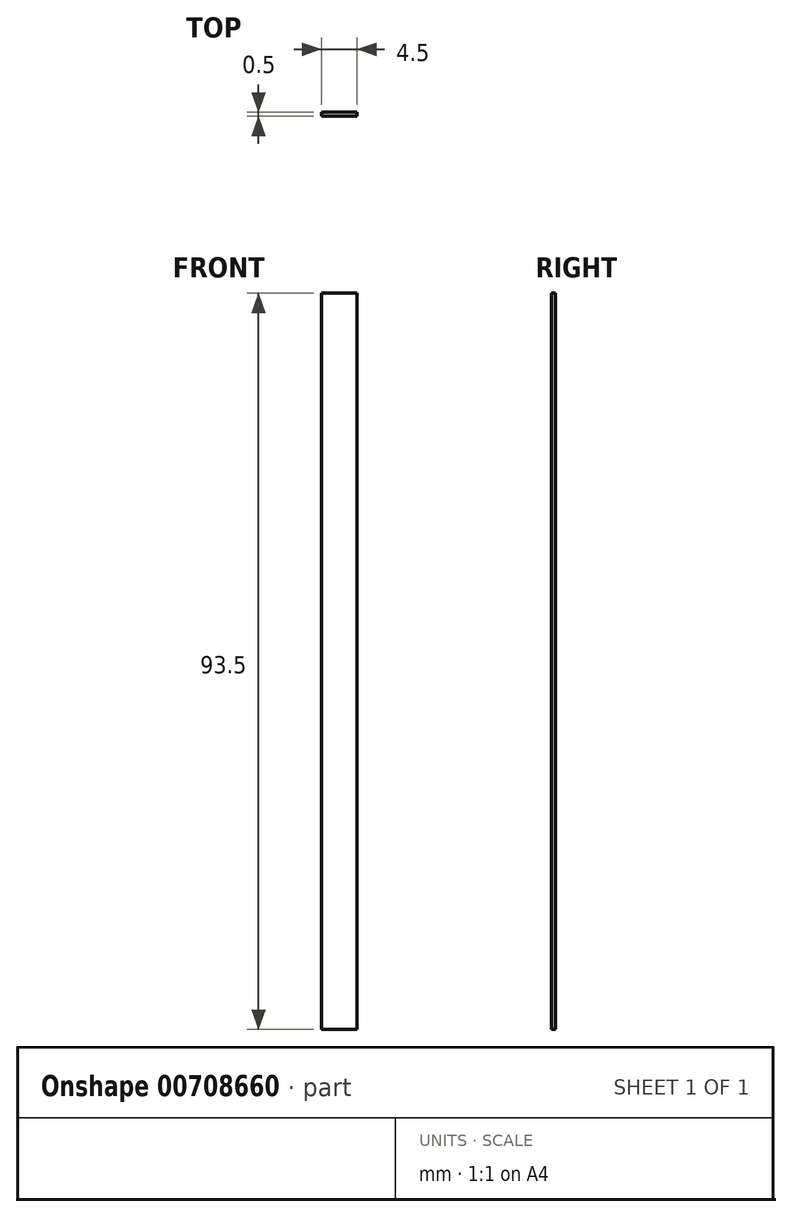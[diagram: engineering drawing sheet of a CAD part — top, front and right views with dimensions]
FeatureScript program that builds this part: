
annotation { "Feature Type Name" : "Feature", "Feature Type Description" : "" }
export const myFeature = defineFeature(function(context is Context, id is Id, definition is map)
    precondition{}
    {
        {
            var Q0;
            Q0=qCreatedBy(makeId("Front.planeOp"),FACE);
            var sketch = newSketch(context, id + "F0", { "sketchPlane" : qUnion([Q0])});
            skLineSegment(sketch, "E0.bottom", {"start": v(-2.36, 68.54) * mm, "end": v(2.14, 68.54) * mm});
            skLineSegment(sketch, "E0.top", {"start": v(-2.36, -24.96) * mm, "end": v(2.14, -24.96) * mm});
            skLineSegment(sketch, "E0.left", {"start": v(-2.36, 68.54) * mm, "end": v(-2.36, -24.96) * mm});
            skLineSegment(sketch, "E0.right", {"start": v(2.14, 68.54) * mm, "end": v(2.14, -24.96) * mm});
            skSolve(sketch);
        }
        {
            var Q0;
            Q0=qSketchRegion(id+"F0",true);
            extrude(context, id + "F1", {"entities" : qUnion([Q0]), "depth" : 0.5 * mm, "offsetDistance" : 25 * mm});
        }
    });
